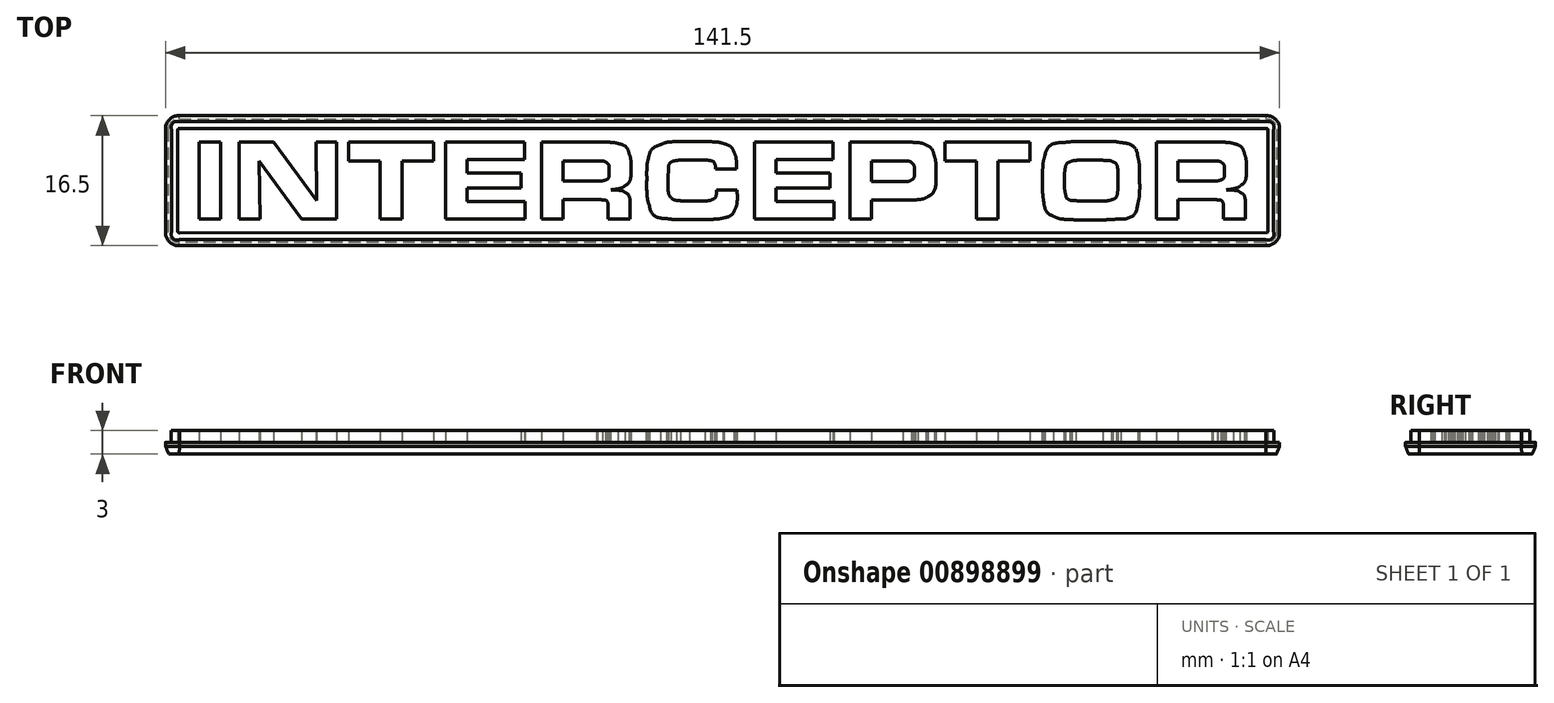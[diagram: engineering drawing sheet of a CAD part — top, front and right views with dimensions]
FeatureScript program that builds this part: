
annotation { "Feature Type Name" : "Feature", "Feature Type Description" : "" }
export const myFeature = defineFeature(function(context is Context, id is Id, definition is map)
    precondition{}
    {
        {
            var Q0;
            Q0=qCreatedBy(makeId("Top.planeOp"),FACE);
            var sketch = newSketch(context, id + "F0", { "sketchPlane" : qUnion([Q0])});
            skLineSegment(sketch, "E0", {"start": v(-66.52, -4.88) * mm, "end": v(-66.52, 4.88) * mm});
            skLineSegment(sketch, "E1", {"start": v(-66.52, 4.88) * mm, "end": v(-63.77, 4.88) * mm});
            skLineSegment(sketch, "E2", {"start": v(-63.77, 4.88) * mm, "end": v(-63.77, -4.88) * mm});
            skLineSegment(sketch, "E3", {"start": v(-63.77, -4.88) * mm, "end": v(-66.52, -4.88) * mm});
            skLineSegment(sketch, "E4", {"start": v(-61.41, -4.88) * mm, "end": v(-61.41, 4.88) * mm});
            skLineSegment(sketch, "E5", {"start": v(-61.41, 4.88) * mm, "end": v(-57.04, 4.88) * mm});
            skLineSegment(sketch, "E6", {"start": v(-57.04, 4.88) * mm, "end": v(-51.57, -2.55) * mm});
            skLineSegment(sketch, "E7", {"start": v(-51.57, -2.55) * mm, "end": v(-51.64, 4.88) * mm});
            skLineSegment(sketch, "E8", {"start": v(-51.64, 4.88) * mm, "end": v(-49.05, 4.88) * mm});
            skLineSegment(sketch, "E9", {"start": v(-49.05, 4.88) * mm, "end": v(-49.05, -4.88) * mm});
            skLineSegment(sketch, "E10", {"start": v(-49.05, -4.88) * mm, "end": v(-53.46, -4.88) * mm});
            skLineSegment(sketch, "E11", {"start": v(-53.46, -4.88) * mm, "end": v(-58.85, 2.47) * mm});
            skLineSegment(sketch, "E12", {"start": v(-58.85, 2.47) * mm, "end": v(-58.77, -4.88) * mm});
            skLineSegment(sketch, "E13", {"start": v(-58.77, -4.88) * mm, "end": v(-61.41, -4.88) * mm});
            skLineSegment(sketch, "E14", {"start": v(-43.47, -4.88) * mm, "end": v(-43.47, 2.47) * mm});
            skLineSegment(sketch, "E15", {"start": v(-43.47, 2.47) * mm, "end": v(-47.5, 2.47) * mm});
            skLineSegment(sketch, "E16", {"start": v(-47.5, 2.47) * mm, "end": v(-47.5, 4.88) * mm});
            skLineSegment(sketch, "E17", {"start": v(-47.5, 4.88) * mm, "end": v(-36.7, 4.88) * mm});
            skLineSegment(sketch, "E18", {"start": v(-36.7, 4.88) * mm, "end": v(-36.7, 2.47) * mm});
            skLineSegment(sketch, "E19", {"start": v(-36.7, 2.47) * mm, "end": v(-40.72, 2.47) * mm});
            skLineSegment(sketch, "E20", {"start": v(-40.72, 2.47) * mm, "end": v(-40.72, -4.88) * mm});
            skLineSegment(sketch, "E21", {"start": v(-40.72, -4.88) * mm, "end": v(-43.47, -4.88) * mm});
            skLineSegment(sketch, "E22", {"start": v(-35.16, 4.88) * mm, "end": v(-25.16, 4.88) * mm});
            skLineSegment(sketch, "E23", {"start": v(-25.16, 4.88) * mm, "end": v(-25.16, 2.66) * mm});
            skLineSegment(sketch, "E24", {"start": v(-25.16, 2.66) * mm, "end": v(-32.45, 2.66) * mm});
            skLineSegment(sketch, "E25", {"start": v(-32.45, 2.66) * mm, "end": v(-32.45, 1) * mm});
            skLineSegment(sketch, "E26", {"start": v(-32.45, 1) * mm, "end": v(-25.57, 1) * mm});
            skLineSegment(sketch, "E27", {"start": v(-25.57, 1) * mm, "end": v(-25.57, -0.93) * mm});
            skLineSegment(sketch, "E28", {"start": v(-25.57, -0.93) * mm, "end": v(-32.45, -0.93) * mm});
            skLineSegment(sketch, "E29", {"start": v(-32.45, -0.93) * mm, "end": v(-32.45, -2.66) * mm});
            skLineSegment(sketch, "E30", {"start": v(-32.45, -2.66) * mm, "end": v(-25.07, -2.66) * mm});
            skLineSegment(sketch, "E31", {"start": v(-25.07, -2.66) * mm, "end": v(-25.07, -4.88) * mm});
            skLineSegment(sketch, "E32", {"start": v(-25.07, -4.88) * mm, "end": v(-35.16, -4.88) * mm});
            skLineSegment(sketch, "E33", {"start": v(-35.16, -4.88) * mm, "end": v(-35.16, 4.88) * mm});
            skLineSegment(sketch, "E34", {"start": v(-23.02, -4.88) * mm, "end": v(-23.02, 4.88) * mm});
            skLineSegment(sketch, "E35", {"start": v(-23.02, 4.88) * mm, "end": v(-15.23, 4.88) * mm});
            skLineSegment(sketch, "E36", {"start": v(-11.77, -3.33) * mm, "end": v(-11.77, -4.88) * mm});
            skLineSegment(sketch, "E37", {"start": v(-11.77, -4.88) * mm, "end": v(-14.55, -4.88) * mm});
            skLineSegment(sketch, "E38", {"start": v(-14.55, -4.88) * mm, "end": v(-14.55, -3.66) * mm});
            skLineSegment(sketch, "E39", {"start": v(-16.06, -2.41) * mm, "end": v(-20.29, -2.41) * mm});
            skLineSegment(sketch, "E40", {"start": v(-20.29, -2.41) * mm, "end": v(-20.29, -4.88) * mm});
            skLineSegment(sketch, "E41", {"start": v(-20.29, -4.88) * mm, "end": v(-23.02, -4.88) * mm});
            skLineSegment(sketch, "E42", {"start": v(-20.29, -0.02) * mm, "end": v(-15.99, -0.02) * mm});
            skLineSegment(sketch, "E43", {"start": v(-15.9, 2.48) * mm, "end": v(-20.29, 2.48) * mm});
            skLineSegment(sketch, "E44", {"start": v(-20.29, 2.48) * mm, "end": v(-20.29, -0.02) * mm});
            skLineSegment(sketch, "E45", {"start": v(-0.8, -1.2) * mm, "end": v(1.86, -1.2) * mm});
            skLineSegment(sketch, "E46", {"start": v(1.86, -1.2) * mm, "end": v(1.86, -1.65) * mm});
            skLineSegment(sketch, "E47", {"start": v(1.75, 1.8) * mm, "end": v(1.75, 1.46) * mm});
            skLineSegment(sketch, "E48", {"start": v(1.75, 1.46) * mm, "end": v(-0.88, 1.46) * mm});
            skLineSegment(sketch, "E49", {"start": v(4.05, 4.88) * mm, "end": v(14.05, 4.88) * mm});
            skLineSegment(sketch, "E50", {"start": v(14.05, 4.88) * mm, "end": v(14.05, 2.66) * mm});
            skLineSegment(sketch, "E51", {"start": v(14.05, 2.66) * mm, "end": v(6.76, 2.66) * mm});
            skLineSegment(sketch, "E52", {"start": v(6.76, 2.66) * mm, "end": v(6.76, 1) * mm});
            skLineSegment(sketch, "E53", {"start": v(6.76, 1) * mm, "end": v(13.64, 1) * mm});
            skLineSegment(sketch, "E54", {"start": v(13.64, 1) * mm, "end": v(13.64, -0.93) * mm});
            skLineSegment(sketch, "E55", {"start": v(13.64, -0.93) * mm, "end": v(6.76, -0.93) * mm});
            skLineSegment(sketch, "E56", {"start": v(6.76, -0.93) * mm, "end": v(6.76, -2.66) * mm});
            skLineSegment(sketch, "E57", {"start": v(6.76, -2.66) * mm, "end": v(14.15, -2.66) * mm});
            skLineSegment(sketch, "E58", {"start": v(14.15, -2.66) * mm, "end": v(14.15, -4.88) * mm});
            skLineSegment(sketch, "E59", {"start": v(14.15, -4.88) * mm, "end": v(4.05, -4.88) * mm});
            skLineSegment(sketch, "E60", {"start": v(4.05, -4.88) * mm, "end": v(4.05, 4.88) * mm});
            skLineSegment(sketch, "E61", {"start": v(16.19, -4.88) * mm, "end": v(16.19, 4.88) * mm});
            skLineSegment(sketch, "E62", {"start": v(16.19, 4.88) * mm, "end": v(23.1, 4.88) * mm});
            skLineSegment(sketch, "E63", {"start": v(23.34, -2.48) * mm, "end": v(18.92, -2.48) * mm});
            skLineSegment(sketch, "E64", {"start": v(18.92, -2.48) * mm, "end": v(18.92, -4.88) * mm});
            skLineSegment(sketch, "E65", {"start": v(18.92, -4.88) * mm, "end": v(16.19, -4.88) * mm});
            skLineSegment(sketch, "E66", {"start": v(18.92, -0.1) * mm, "end": v(22.92, -0.1) * mm});
            skLineSegment(sketch, "E67", {"start": v(22.92, 2.5) * mm, "end": v(18.92, 2.5) * mm});
            skLineSegment(sketch, "E68", {"start": v(18.92, 2.5) * mm, "end": v(18.92, -0.1) * mm});
            skLineSegment(sketch, "E69", {"start": v(32.25, -4.88) * mm, "end": v(32.25, 2.47) * mm});
            skLineSegment(sketch, "E70", {"start": v(32.25, 2.47) * mm, "end": v(28.23, 2.47) * mm});
            skLineSegment(sketch, "E71", {"start": v(28.23, 2.47) * mm, "end": v(28.23, 4.88) * mm});
            skLineSegment(sketch, "E72", {"start": v(28.23, 4.88) * mm, "end": v(39.02, 4.88) * mm});
            skLineSegment(sketch, "E73", {"start": v(39.02, 4.88) * mm, "end": v(39.02, 2.47) * mm});
            skLineSegment(sketch, "E74", {"start": v(39.02, 2.47) * mm, "end": v(35, 2.47) * mm});
            skLineSegment(sketch, "E75", {"start": v(35, 2.47) * mm, "end": v(35, -4.88) * mm});
            skLineSegment(sketch, "E76", {"start": v(35, -4.88) * mm, "end": v(32.25, -4.88) * mm});
            skLineSegment(sketch, "E77", {"start": v(55.13, -4.88) * mm, "end": v(55.13, 4.88) * mm});
            skLineSegment(sketch, "E78", {"start": v(55.13, 4.88) * mm, "end": v(62.93, 4.88) * mm});
            skLineSegment(sketch, "E79", {"start": v(66.4, -3.33) * mm, "end": v(66.4, -4.88) * mm});
            skLineSegment(sketch, "E80", {"start": v(66.4, -4.88) * mm, "end": v(63.6, -4.88) * mm});
            skLineSegment(sketch, "E81", {"start": v(63.6, -4.88) * mm, "end": v(63.6, -3.66) * mm});
            skLineSegment(sketch, "E82", {"start": v(62.1, -2.41) * mm, "end": v(57.87, -2.41) * mm});
            skLineSegment(sketch, "E83", {"start": v(57.87, -2.41) * mm, "end": v(57.87, -4.88) * mm});
            skLineSegment(sketch, "E84", {"start": v(57.87, -4.88) * mm, "end": v(55.13, -4.88) * mm});
            skLineSegment(sketch, "E85", {"start": v(57.87, -0.02) * mm, "end": v(62.17, -0.02) * mm});
            skLineSegment(sketch, "E86", {"start": v(62.27, 2.48) * mm, "end": v(57.87, 2.48) * mm});
            skLineSegment(sketch, "E87", {"start": v(57.87, 2.48) * mm, "end": v(57.87, -0.02) * mm});
            skLineSegment(sketch, "E88", {"start": v(-69, 7.5) * mm, "end": v(69, 7.5) * mm});
            skLineSegment(sketch, "E89", {"start": v(70, 6.5) * mm, "end": v(70, -6.5) * mm});
            skLineSegment(sketch, "E90", {"start": v(69, -7.5) * mm, "end": v(-69, -7.5) * mm});
            skLineSegment(sketch, "E91", {"start": v(-70, -6.5) * mm, "end": v(-70, 6.5) * mm});
            skLineSegment(sketch, "E92", {"start": v(-69, 6.92) * mm, "end": v(69.09, 6.92) * mm});
            skLineSegment(sketch, "E93", {"start": v(69.59, 6.42) * mm, "end": v(69.59, -6.4) * mm});
            skLineSegment(sketch, "E94", {"start": v(69.09, -6.9) * mm, "end": v(-69, -6.92) * mm});
            skLineSegment(sketch, "E95", {"start": v(-69.5, -6.42) * mm, "end": v(-69.5, 6.42) * mm});
            skFitSpline(sketch, "E96", {"points": [v(-15.23, 4.88) * mm, v(-14.33, 4.88) * mm, v(-13.68, 4.82) * mm, v(-13.3, 4.71) * mm]});
            skFitSpline(sketch, "E97", {"points": [v(-13.3, 4.71) * mm, v(-12.58, 4.51) * mm, v(-12.1, 4.1) * mm, v(-11.88, 3.45) * mm]});
            skFitSpline(sketch, "E98", {"points": [v(-11.88, 3.45) * mm, v(-11.72, 3.01) * mm, v(-11.64, 2.43) * mm, v(-11.64, 1.7) * mm]});
            skFitSpline(sketch, "E99", {"points": [v(-11.64, 1.7) * mm, v(-11.64, 0.53) * mm, v(-11.9, -0.26) * mm, v(-12.4, -0.65) * mm]});
            skFitSpline(sketch, "E100", {"points": [v(-12.4, -0.65) * mm, v(-12.68, -0.86) * mm, v(-13.26, -1.03) * mm, v(-14.16, -1.17) * mm]});
            skFitSpline(sketch, "E101", {"points": [v(-14.16, -1.17) * mm, v(-14.05, -1.18) * mm, v(-13.9, -1.19) * mm, v(-13.7, -1.2) * mm]});
            skFitSpline(sketch, "E102", {"points": [v(-13.7, -1.2) * mm, v(-13.07, -1.23) * mm, v(-12.64, -1.32) * mm, v(-12.42, -1.47) * mm]});
            skFitSpline(sketch, "E103", {"points": [v(-12.42, -1.47) * mm, v(-11.98, -1.76) * mm, v(-11.77, -2.38) * mm, v(-11.77, -3.33) * mm]});
            skFitSpline(sketch, "E104", {"points": [v(-14.55, -3.66) * mm, v(-14.55, -2.93) * mm, v(-14.79, -2.52) * mm, v(-15.27, -2.45) * mm]});
            skFitSpline(sketch, "E105", {"points": [v(-15.27, -2.45) * mm, v(-15.42, -2.42) * mm, v(-15.68, -2.41) * mm, v(-16.06, -2.41) * mm]});
            skFitSpline(sketch, "E106", {"points": [v(-15.99, -0.02) * mm, v(-15.42, -0.02) * mm, v(-15.05, 0.02) * mm, v(-14.87, 0.1) * mm]});
            skFitSpline(sketch, "E107", {"points": [v(-14.87, 0.1) * mm, v(-14.56, 0.23) * mm, v(-14.4, 0.56) * mm, v(-14.4, 1.08) * mm]});
            skFitSpline(sketch, "E108", {"points": [v(-14.4, 1.08) * mm, v(-14.4, 1.7) * mm, v(-14.5, 2.09) * mm, v(-14.71, 2.26) * mm]});
            skFitSpline(sketch, "E109", {"points": [v(-14.71, 2.26) * mm, v(-14.9, 2.4) * mm, v(-15.28, 2.48) * mm, v(-15.9, 2.48) * mm]});
            skFitSpline(sketch, "E110", {"points": [v(1.86, -1.65) * mm, v(1.86, -2.56) * mm, v(1.76, -3.22) * mm, v(1.57, -3.64) * mm]});
            skFitSpline(sketch, "E111", {"points": [v(1.57, -3.64) * mm, v(1.31, -4.19) * mm, v(0.82, -4.55) * mm, v(0.09, -4.74) * mm]});
            skFitSpline(sketch, "E112", {"points": [v(0.09, -4.74) * mm, v(-0.28, -4.83) * mm, v(-0.81, -4.89) * mm, v(-1.52, -4.92) * mm]});
            skFitSpline(sketch, "E113", {"points": [v(-1.52, -4.92) * mm, v(-2, -4.94) * mm, v(-2.97, -4.95) * mm, v(-4.4, -4.95) * mm]});
            skFitSpline(sketch, "E114", {"points": [v(-4.4, -4.95) * mm, v(-5.58, -4.95) * mm, v(-6.48, -4.9) * mm, v(-7.1, -4.82) * mm]});
            skFitSpline(sketch, "E115", {"points": [v(-7.1, -4.82) * mm, v(-8.26, -4.66) * mm, v(-9, -4.1) * mm, v(-9.3, -3.13) * mm]});
            skFitSpline(sketch, "E116", {"points": [v(-9.3, -3.13) * mm, v(-9.52, -2.47) * mm, v(-9.62, -1.35) * mm, v(-9.62, 0.23) * mm]});
            skFitSpline(sketch, "E117", {"points": [v(-9.62, 0.23) * mm, v(-9.62, 1.44) * mm, v(-9.56, 2.3) * mm, v(-9.43, 2.78) * mm]});
            skFitSpline(sketch, "E118", {"points": [v(-9.43, 2.78) * mm, v(-9.19, 3.65) * mm, v(-8.68, 4.25) * mm, v(-7.9, 4.57) * mm]});
            skFitSpline(sketch, "E119", {"points": [v(-7.9, 4.57) * mm, v(-7.28, 4.82) * mm, v(-6.04, 4.95) * mm, v(-4.17, 4.95) * mm]});
            skFitSpline(sketch, "E120", {"points": [v(-4.17, 4.95) * mm, v(-1.8, 4.95) * mm, v(-0.37, 4.86) * mm, v(0.16, 4.69) * mm]});
            skFitSpline(sketch, "E121", {"points": [v(0.16, 4.69) * mm, v(0.78, 4.49) * mm, v(1.22, 4.12) * mm, v(1.46, 3.58) * mm]});
            skFitSpline(sketch, "E122", {"points": [v(1.46, 3.58) * mm, v(1.65, 3.16) * mm, v(1.75, 2.57) * mm, v(1.75, 1.8) * mm]});
            skFitSpline(sketch, "E123", {"points": [v(-0.88, 1.46) * mm, v(-0.9, 1.78) * mm, v(-0.95, 2.01) * mm, v(-1.02, 2.15) * mm]});
            skFitSpline(sketch, "E124", {"points": [v(-1.02, 2.15) * mm, v(-1.15, 2.4) * mm, v(-1.55, 2.56) * mm, v(-2.2, 2.6) * mm]});
            skFitSpline(sketch, "E125", {"points": [v(-2.2, 2.6) * mm, v(-2.26, 2.6) * mm, v(-2.7, 2.61) * mm, v(-3.52, 2.61) * mm]});
            skFitSpline(sketch, "E126", {"points": [v(-3.52, 2.61) * mm, v(-4.84, 2.61) * mm, v(-5.61, 2.59) * mm, v(-5.85, 2.54) * mm]});
            skFitSpline(sketch, "E127", {"points": [v(-5.85, 2.54) * mm, v(-6.48, 2.41) * mm, v(-6.83, 1.95) * mm, v(-6.88, 1.17) * mm]});
            skFitSpline(sketch, "E128", {"points": [v(-6.88, 1.17) * mm, v(-6.9, 0.9) * mm, v(-6.9, 0.48) * mm, v(-6.9, -0.1) * mm]});
            skFitSpline(sketch, "E129", {"points": [v(-6.9, -0.1) * mm, v(-6.9, -1.18) * mm, v(-6.78, -1.86) * mm, v(-6.53, -2.13) * mm]});
            skFitSpline(sketch, "E130", {"points": [v(-6.53, -2.13) * mm, v(-6.33, -2.36) * mm, v(-5.93, -2.5) * mm, v(-5.35, -2.55) * mm]});
            skFitSpline(sketch, "E131", {"points": [v(-5.35, -2.55) * mm, v(-5.15, -2.57) * mm, v(-4.72, -2.58) * mm, v(-4.07, -2.58) * mm]});
            skFitSpline(sketch, "E132", {"points": [v(-4.07, -2.58) * mm, v(-2.52, -2.58) * mm, v(-1.6, -2.52) * mm, v(-1.33, -2.39) * mm]});
            skFitSpline(sketch, "E133", {"points": [v(-1.33, -2.39) * mm, v(-0.98, -2.23) * mm, v(-0.8, -1.83) * mm, v(-0.8, -1.2) * mm]});
            skFitSpline(sketch, "E134", {"points": [v(23.1, 4.88) * mm, v(23.85, 4.88) * mm, v(24.31, 4.87) * mm, v(24.5, 4.85) * mm]});
            skFitSpline(sketch, "E135", {"points": [v(24.5, 4.85) * mm, v(25.06, 4.81) * mm, v(25.51, 4.7) * mm, v(25.86, 4.51) * mm]});
            skFitSpline(sketch, "E136", {"points": [v(25.86, 4.51) * mm, v(26.37, 4.24) * mm, v(26.71, 3.78) * mm, v(26.9, 3.14) * mm]});
            skFitSpline(sketch, "E137", {"points": [v(26.9, 3.14) * mm, v(27.04, 2.7) * mm, v(27.1, 2.08) * mm, v(27.1, 1.31) * mm]});
            skFitSpline(sketch, "E138", {"points": [v(27.1, 1.31) * mm, v(27.1, -0.42) * mm, v(26.76, -1.53) * mm, v(26.08, -2) * mm]});
            skFitSpline(sketch, "E139", {"points": [v(26.08, -2) * mm, v(25.77, -2.21) * mm, v(25.35, -2.35) * mm, v(24.82, -2.41) * mm]});
            skFitSpline(sketch, "E140", {"points": [v(24.82, -2.41) * mm, v(24.45, -2.45) * mm, v(23.96, -2.48) * mm, v(23.34, -2.48) * mm]});
            skFitSpline(sketch, "E141", {"points": [v(22.92, -0.1) * mm, v(23.42, -0.1) * mm, v(23.77, -0.04) * mm, v(23.97, 0.08) * mm]});
            skFitSpline(sketch, "E142", {"points": [v(23.97, 0.08) * mm, v(24.23, 0.25) * mm, v(24.36, 0.58) * mm, v(24.36, 1.08) * mm]});
            skFitSpline(sketch, "E143", {"points": [v(24.36, 1.08) * mm, v(24.36, 1.67) * mm, v(24.26, 2.06) * mm, v(24.05, 2.25) * mm]});
            skFitSpline(sketch, "E144", {"points": [v(24.05, 2.25) * mm, v(23.86, 2.41) * mm, v(23.49, 2.5) * mm, v(22.92, 2.5) * mm]});
            skFitSpline(sketch, "E145", {"points": [v(46.42, 4.98) * mm, v(48.72, 4.98) * mm, v(50.12, 4.93) * mm, v(50.63, 4.83) * mm]});
            skFitSpline(sketch, "E146", {"points": [v(50.63, 4.83) * mm, v(51.78, 4.6) * mm, v(52.5, 3.96) * mm, v(52.77, 2.9) * mm]});
            skFitSpline(sketch, "E147", {"points": [v(52.77, 2.9) * mm, v(52.88, 2.52) * mm, v(52.94, 2) * mm, v(52.96, 1.34) * mm]});
            skFitSpline(sketch, "E148", {"points": [v(52.96, 1.34) * mm, v(52.97, 0.96) * mm, v(52.98, 0.49) * mm, v(52.98, -0.07) * mm]});
            skFitSpline(sketch, "E149", {"points": [v(52.98, -0.07) * mm, v(52.98, -1.3) * mm, v(52.9, -2.2) * mm, v(52.77, -2.78) * mm]});
            skFitSpline(sketch, "E150", {"points": [v(52.77, -2.78) * mm, v(52.45, -4.06) * mm, v(51.54, -4.76) * mm, v(50.03, -4.89) * mm]});
            skFitSpline(sketch, "E151", {"points": [v(50.03, -4.89) * mm, v(49.36, -4.95) * mm, v(48.27, -4.98) * mm, v(46.75, -4.98) * mm]});
            skFitSpline(sketch, "E152", {"points": [v(46.75, -4.98) * mm, v(45.44, -4.98) * mm, v(44.65, -4.97) * mm, v(44.37, -4.95) * mm]});
            skFitSpline(sketch, "E153", {"points": [v(44.37, -4.95) * mm, v(43.3, -4.9) * mm, v(42.52, -4.75) * mm, v(42.04, -4.5) * mm]});
            skFitSpline(sketch, "E154", {"points": [v(42.04, -4.5) * mm, v(41.37, -4.16) * mm, v(40.94, -3.47) * mm, v(40.76, -2.44) * mm]});
            skFitSpline(sketch, "E155", {"points": [v(40.76, -2.44) * mm, v(40.69, -2) * mm, v(40.65, -1.18) * mm, v(40.65, 0.03) * mm]});
            skFitSpline(sketch, "E156", {"points": [v(40.65, 0.03) * mm, v(40.65, 0.85) * mm, v(40.66, 1.37) * mm, v(40.67, 1.6) * mm]});
            skFitSpline(sketch, "E157", {"points": [v(40.67, 1.6) * mm, v(40.7, 2.19) * mm, v(40.8, 2.7) * mm, v(40.94, 3.12) * mm]});
            skFitSpline(sketch, "E158", {"points": [v(40.94, 3.12) * mm, v(41.3, 4.13) * mm, v(42.16, 4.72) * mm, v(43.55, 4.87) * mm]});
            skFitSpline(sketch, "E159", {"points": [v(43.55, 4.87) * mm, v(44.21, 4.94) * mm, v(45.17, 4.98) * mm, v(46.42, 4.98) * mm]});
            skFitSpline(sketch, "E160", {"points": [v(46.8, 2.6) * mm, v(45.35, 2.6) * mm, v(44.45, 2.52) * mm, v(44.1, 2.37) * mm]});
            skFitSpline(sketch, "E161", {"points": [v(44.1, 2.37) * mm, v(43.8, 2.23) * mm, v(43.59, 1.89) * mm, v(43.5, 1.35) * mm]});
            skFitSpline(sketch, "E162", {"points": [v(43.5, 1.35) * mm, v(43.45, 1.13) * mm, v(43.43, 0.7) * mm, v(43.43, 0.07) * mm]});
            skFitSpline(sketch, "E163", {"points": [v(43.43, 0.07) * mm, v(43.43, -0.76) * mm, v(43.48, -1.34) * mm, v(43.57, -1.69) * mm]});
            skFitSpline(sketch, "E164", {"points": [v(43.57, -1.69) * mm, v(43.7, -2.2) * mm, v(44.15, -2.49) * mm, v(44.88, -2.55) * mm]});
            skFitSpline(sketch, "E165", {"points": [v(44.88, -2.55) * mm, v(45.3, -2.58) * mm, v(45.83, -2.6) * mm, v(46.44, -2.6) * mm]});
            skFitSpline(sketch, "E166", {"points": [v(46.44, -2.6) * mm, v(48.07, -2.6) * mm, v(49.07, -2.53) * mm, v(49.43, -2.41) * mm]});
            skFitSpline(sketch, "E167", {"points": [v(49.43, -2.41) * mm, v(49.83, -2.27) * mm, v(50.08, -1.91) * mm, v(50.19, -1.33) * mm]});
            skFitSpline(sketch, "E168", {"points": [v(50.19, -1.33) * mm, v(50.23, -1.11) * mm, v(50.25, -0.63) * mm, v(50.25, 0.13) * mm]});
            skFitSpline(sketch, "E169", {"points": [v(50.25, 0.13) * mm, v(50.25, 0.71) * mm, v(50.24, 1.1) * mm, v(50.2, 1.3) * mm]});
            skFitSpline(sketch, "E170", {"points": [v(50.2, 1.3) * mm, v(50.13, 1.87) * mm, v(49.92, 2.23) * mm, v(49.58, 2.4) * mm]});
            skFitSpline(sketch, "E171", {"points": [v(49.58, 2.4) * mm, v(49.37, 2.5) * mm, v(48.95, 2.56) * mm, v(48.3, 2.59) * mm]});
            skFitSpline(sketch, "E172", {"points": [v(48.3, 2.59) * mm, v(48.2, 2.6) * mm, v(47.7, 2.6) * mm, v(46.8, 2.6) * mm]});
            skFitSpline(sketch, "E173", {"points": [v(62.93, 4.88) * mm, v(63.83, 4.88) * mm, v(64.47, 4.82) * mm, v(64.86, 4.71) * mm]});
            skFitSpline(sketch, "E174", {"points": [v(64.86, 4.71) * mm, v(65.58, 4.51) * mm, v(66.05, 4.1) * mm, v(66.28, 3.45) * mm]});
            skFitSpline(sketch, "E175", {"points": [v(66.28, 3.45) * mm, v(66.44, 3.01) * mm, v(66.52, 2.43) * mm, v(66.52, 1.7) * mm]});
            skFitSpline(sketch, "E176", {"points": [v(66.52, 1.7) * mm, v(66.52, 0.53) * mm, v(66.26, -0.26) * mm, v(65.75, -0.65) * mm]});
            skFitSpline(sketch, "E177", {"points": [v(65.75, -0.65) * mm, v(65.48, -0.86) * mm, v(64.9, -1.03) * mm, v(64, -1.17) * mm]});
            skFitSpline(sketch, "E178", {"points": [v(64, -1.17) * mm, v(64.1, -1.18) * mm, v(64.25, -1.19) * mm, v(64.45, -1.2) * mm]});
            skFitSpline(sketch, "E179", {"points": [v(64.45, -1.2) * mm, v(65.1, -1.23) * mm, v(65.52, -1.32) * mm, v(65.74, -1.47) * mm]});
            skFitSpline(sketch, "E180", {"points": [v(65.74, -1.47) * mm, v(66.17, -1.76) * mm, v(66.4, -2.38) * mm, v(66.4, -3.33) * mm]});
            skFitSpline(sketch, "E181", {"points": [v(63.6, -3.66) * mm, v(63.6, -2.93) * mm, v(63.37, -2.52) * mm, v(62.89, -2.45) * mm]});
            skFitSpline(sketch, "E182", {"points": [v(62.89, -2.45) * mm, v(62.74, -2.42) * mm, v(62.47, -2.41) * mm, v(62.1, -2.41) * mm]});
            skFitSpline(sketch, "E183", {"points": [v(62.17, -0.02) * mm, v(62.74, -0.02) * mm, v(63.11, 0.02) * mm, v(63.3, 0.1) * mm]});
            skFitSpline(sketch, "E184", {"points": [v(63.3, 0.1) * mm, v(63.6, 0.23) * mm, v(63.75, 0.56) * mm, v(63.75, 1.08) * mm]});
            skFitSpline(sketch, "E185", {"points": [v(63.75, 1.08) * mm, v(63.75, 1.7) * mm, v(63.65, 2.09) * mm, v(63.44, 2.26) * mm]});
            skFitSpline(sketch, "E186", {"points": [v(63.44, 2.26) * mm, v(63.27, 2.4) * mm, v(62.87, 2.48) * mm, v(62.27, 2.48) * mm]});
            skFitSpline(sketch, "E187", {"points": [v(69, 7.5) * mm, v(69.55, 7.5) * mm, v(70, 7.05) * mm, v(70, 6.5) * mm]});
            skFitSpline(sketch, "E188", {"points": [v(70, -6.5) * mm, v(70, -7.05) * mm, v(69.55, -7.5) * mm, v(69, -7.5) * mm]});
            skFitSpline(sketch, "E189", {"points": [v(-69, -7.5) * mm, v(-69.55, -7.5) * mm, v(-70, -7.05) * mm, v(-70, -6.5) * mm]});
            skFitSpline(sketch, "E190", {"points": [v(-70, 6.5) * mm, v(-70, 7.05) * mm, v(-69.55, 7.5) * mm, v(-69, 7.5) * mm]});
            skFitSpline(sketch, "E191", {"points": [v(69.08, 6.92) * mm, v(69.36, 6.92) * mm, v(69.58, 6.7) * mm, v(69.59, 6.42) * mm]});
            skFitSpline(sketch, "E192", {"points": [v(69.59, -6.4) * mm, v(69.59, -6.68) * mm, v(69.36, -6.9) * mm, v(69.09, -6.9) * mm]});
            skFitSpline(sketch, "E193", {"points": [v(-69, -6.92) * mm, v(-69.28, -6.92) * mm, v(-69.5, -6.7) * mm, v(-69.5, -6.42) * mm]});
            skFitSpline(sketch, "E194", {"points": [v(-69.5, 6.42) * mm, v(-69.5, 6.7) * mm, v(-69.28, 6.92) * mm, v(-69, 6.92) * mm]});
            skFitSpline(sketch, "E195.0", {"points": [v(-70.75, 6.5) * mm, v(-70.75, 6.74) * mm, v(-70.65, 7.2) * mm, v(-70.27, 7.77) * mm, v(-69.7, 8.15) * mm, v(-69.24, 8.25) * mm, v(-69, 8.25) * mm]});
            skLineSegment(sketch, "E195.1", {"start": v(-70.75, -6.5) * mm, "end": v(-70.75, 6.5) * mm});
            skLineSegment(sketch, "E195.2", {"start": v(-69, 8.25) * mm, "end": v(69, 8.25) * mm});
            skFitSpline(sketch, "E195.3", {"points": [v(-69, -8.25) * mm, v(-69.24, -8.25) * mm, v(-69.7, -8.15) * mm, v(-70.27, -7.77) * mm, v(-70.65, -7.2) * mm, v(-70.75, -6.74) * mm, v(-70.75, -6.5) * mm]});
            skFitSpline(sketch, "E195.4", {"points": [v(69, 8.25) * mm, v(69.24, 8.25) * mm, v(69.7, 8.15) * mm, v(70.27, 7.77) * mm, v(70.65, 7.2) * mm, v(70.75, 6.74) * mm, v(70.75, 6.5) * mm]});
            skLineSegment(sketch, "E195.5", {"start": v(70.75, 6.5) * mm, "end": v(70.75, -6.5) * mm});
            skFitSpline(sketch, "E195.6", {"points": [v(70.75, -6.5) * mm, v(70.75, -6.74) * mm, v(70.65, -7.2) * mm, v(70.27, -7.77) * mm, v(69.7, -8.15) * mm, v(69.24, -8.25) * mm, v(69, -8.25) * mm]});
            skLineSegment(sketch, "E195.7", {"start": v(69, -8.25) * mm, "end": v(-69, -8.25) * mm});
            skFitSpline(sketch, "E196.0", {"points": [v(-69.2, 6.42) * mm, v(-69.2, 6.48) * mm, v(-69.16, 6.57) * mm, v(-69.06, 6.62) * mm, v(-69, 6.62) * mm]});
            skLineSegment(sketch, "E196.1", {"start": v(-69.2, -6.42) * mm, "end": v(-69.2, 6.42) * mm});
            skLineSegment(sketch, "E196.2", {"start": v(-69, 6.62) * mm, "end": v(69.09, 6.62) * mm});
            skFitSpline(sketch, "E196.3", {"points": [v(-69, -6.62) * mm, v(-69.06, -6.62) * mm, v(-69.15, -6.57) * mm, v(-69.2, -6.48) * mm, v(-69.2, -6.42) * mm]});
            skFitSpline(sketch, "E196.4", {"points": [v(69.08, 6.62) * mm, v(69.14, 6.62) * mm, v(69.24, 6.57) * mm, v(69.29, 6.48) * mm, v(69.29, 6.42) * mm]});
            skLineSegment(sketch, "E196.5", {"start": v(69.29, 6.42) * mm, "end": v(69.29, -6.4) * mm});
            skFitSpline(sketch, "E196.6", {"points": [v(69.29, -6.4) * mm, v(69.29, -6.46) * mm, v(69.24, -6.56) * mm, v(69.14, -6.6) * mm, v(69.09, -6.6) * mm]});
            skLineSegment(sketch, "E196.7", {"start": v(69.09, -6.6) * mm, "end": v(-69, -6.62) * mm});
            skSolve(sketch);
        }
        {
            var Q0;
            Q0=makeQuery(id+"F0.imprint","IMPRINT",FACE,{"disambiguationData":[TD([[makeQuery(id+"F0.imprint","IMPRINT",EDGE,{"derivedFrom":sQuery(id+"F0.wireOp",EDGE,"E42")}),1.0]])]});
            var Q1;
            Q1=makeQuery(id+"F0.imprint","IMPRINT",FACE,{"disambiguationData":[TD([[makeQuery(id+"F0.imprint","IMPRINT",EDGE,{"derivedFrom":sQuery(id+"F0.wireOp",EDGE,"E77")}),-1.0]])]});
            var Q2;
            Q2=makeQuery(id+"F0.imprint","IMPRINT",FACE,{"disambiguationData":[TD([[makeQuery(id+"F0.imprint","IMPRINT",EDGE,{"derivedFrom":sQuery(id+"F0.wireOp",EDGE,"E45")}),-1.0]])]});
            var Q3;
            Q3=makeQuery(id+"F0.imprint","IMPRINT",FACE,{"disambiguationData":[TD([[makeQuery(id+"F0.imprint","IMPRINT",EDGE,{"derivedFrom":sQuery(id+"F0.wireOp",EDGE,"E0")}),-1.0]])]});
            var Q4;
            Q4=makeQuery(id+"F0.imprint","IMPRINT",FACE,{"disambiguationData":[TD([[makeQuery(id+"F0.imprint","IMPRINT",EDGE,{"derivedFrom":sQuery(id+"F0.wireOp",EDGE,"E14")}),-1.0]])]});
            var Q5;
            Q5=makeQuery(id+"F0.imprint","IMPRINT",FACE,{"disambiguationData":[TD([[makeQuery(id+"F0.imprint","IMPRINT",EDGE,{"derivedFrom":sQuery(id+"F0.wireOp",EDGE,"E34")}),-1.0]])]});
            var Q6;
            Q6=makeQuery(id+"F0.imprint","IMPRINT",FACE,{"disambiguationData":[TD([[makeQuery(id+"F0.imprint","IMPRINT",EDGE,{"derivedFrom":sQuery(id+"F0.wireOp",EDGE,"E66")}),1.0]])]});
            var Q7;
            Q7=makeQuery(id+"F0.imprint","IMPRINT",FACE,{"disambiguationData":[TD([[makeQuery(id+"F0.imprint","IMPRINT",EDGE,{"derivedFrom":sQuery(id+"F0.wireOp",EDGE,"E85")}),1.0]])]});
            var Q8;
            Q8=makeQuery(id+"F0.imprint","IMPRINT",FACE,{"disambiguationData":[TD([[makeQuery(id+"F0.imprint","IMPRINT",EDGE,{"derivedFrom":sQuery(id+"F0.wireOp",EDGE,"E160")}),1.0]])]});
            var Q9;
            Q9=makeQuery(id+"F0.imprint","IMPRINT",FACE,{"disambiguationData":[TD([[makeQuery(id+"F0.imprint","IMPRINT",EDGE,{"derivedFrom":sQuery(id+"F0.wireOp",EDGE,"E69")}),-1.0]])]});
            var Q10;
            Q10=makeQuery(id+"F0.imprint","IMPRINT",FACE,{"disambiguationData":[TD([[makeQuery(id+"F0.imprint","IMPRINT",EDGE,{"derivedFrom":sQuery(id+"F0.wireOp",EDGE,"E4")}),-1.0]])]});
            var Q11;
            Q11=makeQuery(id+"F0.imprint","IMPRINT",FACE,{"disambiguationData":[TD([[makeQuery(id+"F0.imprint","IMPRINT",EDGE,{"derivedFrom":sQuery(id+"F0.wireOp",EDGE,"E22")}),-1.0]])]});
            var Q12;
            Q12=makeQuery(id+"F0.imprint","IMPRINT",FACE,{"disambiguationData":[TD([[makeQuery(id+"F0.imprint","IMPRINT",EDGE,{"derivedFrom":sQuery(id+"F0.wireOp",EDGE,"E61")}),-1.0]])]});
            var Q13;
            Q13=makeQuery(id+"F0.imprint","IMPRINT",FACE,{"disambiguationData":[TD([[makeQuery(id+"F0.imprint","IMPRINT",EDGE,{"derivedFrom":sQuery(id+"F0.wireOp",EDGE,"E88")}),-1.0]])]});
            var Q14;
            Q14=makeQuery(id+"F0.imprint","IMPRINT",FACE,{"disambiguationData":[TD([[makeQuery(id+"F0.imprint","IMPRINT",EDGE,{"derivedFrom":sQuery(id+"F0.wireOp",EDGE,"E49")}),-1.0]])]});
            var Q15;
            Q15=makeQuery(id+"F0.imprint","IMPRINT",FACE,{"disambiguationData":[TD([[makeQuery(id+"F0.imprint","IMPRINT",EDGE,{"derivedFrom":sQuery(id+"F0.wireOp",EDGE,"E88")}),1.0]])]});
            var Q16;
            Q16=makeQuery(id+"F0.imprint","IMPRINT",FACE,{"disambiguationData":[TD([[makeQuery(id+"F0.imprint","IMPRINT",EDGE,{"derivedFrom":sQuery(id+"F0.wireOp",EDGE,"E92")}),-1.0]])]});
            var Q17;
            Q17=makeQuery(id+"F0.imprint","IMPRINT",FACE,{"disambiguationData":[TD([[makeQuery(id+"F0.imprint","IMPRINT",EDGE,{"derivedFrom":sQuery(id+"F0.wireOp",EDGE,"E0")}),1.0]])]});
            var Q18;
            Q18=makeQuery(id+"F0.imprint","IMPRINT",FACE,{"disambiguationData":[TD([[makeQuery(id+"F0.imprint","IMPRINT",EDGE,{"derivedFrom":sQuery(id+"F0.wireOp",EDGE,"E145")}),-1.0]])]});
            extrude(context, id + "F1", {"entities" : qUnion([Q0, Q1, Q2, Q3, Q4, Q5, Q6, Q7, Q8, Q9, Q10, Q11, Q12, Q13, Q14, Q15, Q16, Q17, Q18]), "oppositeDirection" : true, "depth" : 1.5 * mm, "offsetDistance" : 25 * mm});
        }
        {
            var Q0;
            Q0=makeQuery(id+"F0.imprint","IMPRINT",FACE,{"disambiguationData":[TD([[makeQuery(id+"F0.imprint","IMPRINT",EDGE,{"derivedFrom":sQuery(id+"F0.wireOp",EDGE,"E0")}),-1.0]])]});
            var Q1;
            Q1=makeQuery(id+"F0.imprint","IMPRINT",FACE,{"disambiguationData":[TD([[makeQuery(id+"F0.imprint","IMPRINT",EDGE,{"derivedFrom":sQuery(id+"F0.wireOp",EDGE,"E4")}),-1.0]])]});
            var Q2;
            Q2=makeQuery(id+"F0.imprint","IMPRINT",FACE,{"disambiguationData":[TD([[makeQuery(id+"F0.imprint","IMPRINT",EDGE,{"derivedFrom":sQuery(id+"F0.wireOp",EDGE,"E14")}),-1.0]])]});
            var Q3;
            Q3=makeQuery(id+"F0.imprint","IMPRINT",FACE,{"disambiguationData":[TD([[makeQuery(id+"F0.imprint","IMPRINT",EDGE,{"derivedFrom":sQuery(id+"F0.wireOp",EDGE,"E22")}),-1.0]])]});
            var Q4;
            Q4=makeQuery(id+"F0.imprint","IMPRINT",FACE,{"disambiguationData":[TD([[makeQuery(id+"F0.imprint","IMPRINT",EDGE,{"derivedFrom":sQuery(id+"F0.wireOp",EDGE,"E34")}),-1.0]])]});
            var Q5;
            Q5=makeQuery(id+"F0.imprint","IMPRINT",FACE,{"disambiguationData":[TD([[makeQuery(id+"F0.imprint","IMPRINT",EDGE,{"derivedFrom":sQuery(id+"F0.wireOp",EDGE,"E45")}),-1.0]])]});
            var Q6;
            Q6=makeQuery(id+"F0.imprint","IMPRINT",FACE,{"disambiguationData":[TD([[makeQuery(id+"F0.imprint","IMPRINT",EDGE,{"derivedFrom":sQuery(id+"F0.wireOp",EDGE,"E49")}),-1.0]])]});
            var Q7;
            Q7=makeQuery(id+"F0.imprint","IMPRINT",FACE,{"disambiguationData":[TD([[makeQuery(id+"F0.imprint","IMPRINT",EDGE,{"derivedFrom":sQuery(id+"F0.wireOp",EDGE,"E61")}),-1.0]])]});
            var Q8;
            Q8=makeQuery(id+"F0.imprint","IMPRINT",FACE,{"disambiguationData":[TD([[makeQuery(id+"F0.imprint","IMPRINT",EDGE,{"derivedFrom":sQuery(id+"F0.wireOp",EDGE,"E69")}),-1.0]])]});
            var Q9;
            Q9=makeQuery(id+"F0.imprint","IMPRINT",FACE,{"disambiguationData":[TD([[makeQuery(id+"F0.imprint","IMPRINT",EDGE,{"derivedFrom":sQuery(id+"F0.wireOp",EDGE,"E77")}),-1.0]])]});
            var Q10;
            Q10=makeQuery(id+"F0.imprint","IMPRINT",FACE,{"disambiguationData":[TD([[makeQuery(id+"F0.imprint","IMPRINT",EDGE,{"derivedFrom":sQuery(id+"F0.wireOp",EDGE,"E88")}),-1.0]])]});
            var Q11;
            Q11=makeQuery(id+"F0.imprint","IMPRINT",FACE,{"disambiguationData":[TD([[makeQuery(id+"F0.imprint","IMPRINT",EDGE,{"derivedFrom":sQuery(id+"F0.wireOp",EDGE,"E92")}),-1.0]])]});
            var Q12;
            Q12=makeQuery(id+"F0.imprint","IMPRINT",FACE,{"disambiguationData":[TD([[makeQuery(id+"F0.imprint","IMPRINT",EDGE,{"derivedFrom":sQuery(id+"F0.wireOp",EDGE,"E145")}),-1.0]])]});
            extrude(context, id + "F2", {"entities" : qUnion([Q0, Q1, Q2, Q3, Q4, Q5, Q6, Q7, Q8, Q9, Q10, Q11, Q12]), "operationType" : NewBodyOperationType.ADD, "depth" : 1.5 * mm, "offsetDistance" : 25 * mm});
        }
        {
            var Q0;
            Q0=makeQuery(id+"F1.opExtrude","CAP_FACE",FACE,{"disambiguationData":[OSD([sQuery(id+"F0.wireOp",EDGE,"E195.0"),sQuery(id+"F0.wireOp",EDGE,"E195.1"),sQuery(id+"F0.wireOp",EDGE,"E195.2"),sQuery(id+"F0.wireOp",EDGE,"E195.3"),sQuery(id+"F0.wireOp",EDGE,"E195.4"),sQuery(id+"F0.wireOp",EDGE,"E195.5"),sQuery(id+"F0.wireOp",EDGE,"E195.6"),sQuery(id+"F0.wireOp",EDGE,"E195.7")])],"isStart":false});
            chamfer(context, id + "F3", {"entities" : qUnion([Q0]), "chamferType" : ChamferType.TWO_OFFSETS, "width1" : .4 * mm, "oppositeDirection" : false, "width2" : 1 * mm, "tangentPropagation" : true});
        }
    });
